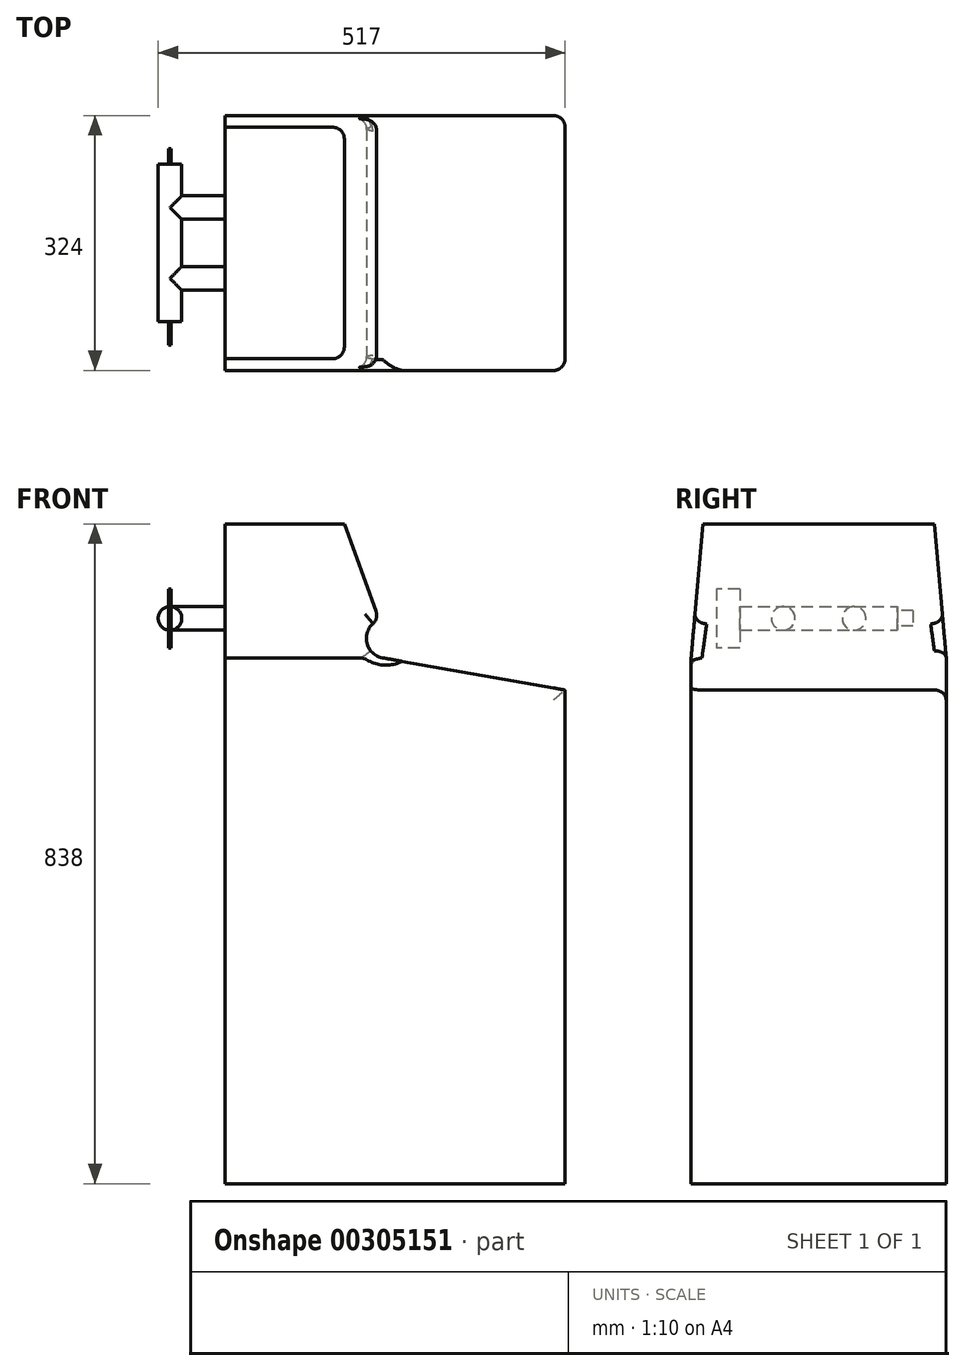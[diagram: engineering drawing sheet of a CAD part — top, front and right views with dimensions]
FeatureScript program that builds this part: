
annotation { "Feature Type Name" : "Feature", "Feature Type Description" : "" }
export const myFeature = defineFeature(function(context is Context, id is Id, definition is map)
    precondition{}
    {
        {
            var Q0;
            Q0=qCreatedBy(makeId("Top.planeOp"),FACE);
            var sketch = newSketch(context, id + "F0", { "sketchPlane" : qUnion([Q0])});
            skLineSegment(sketch, "E0.bottom", {"start": v(0, 162) * mm, "end": v(432, 162) * mm});
            skLineSegment(sketch, "E0.top", {"start": v(0, -162) * mm, "end": v(432, -162) * mm});
            skLineSegment(sketch, "E0.left", {"start": v(0, 162) * mm, "end": v(0, -162) * mm});
            skLineSegment(sketch, "E0.right", {"start": v(432, 162) * mm, "end": v(432, -162) * mm});
            skSolve(sketch);
        }
        {
            var Q0;
            Q0 = qSketchRegion(id + "F0", true);
            extrude(context, id + "F1", {"entities" : qUnion([Q0]), "depth" : 838 * mm});
        }
        {
            var Q0;
            Q0=makeQuery(id+"F1.opExtrude","SWEPT_FACE",FACE,{"disambiguationData":[OSD([sQuery(id+"F0.wireOp",EDGE,"E0.top")])]});
            var sketch = newSketch(context, id + "F2", { "sketchPlane" : qUnion([Q0])});
            skLineSegment(sketch, "E1", {"start": v(200, 668) * mm, "end": v(432, 627.1) * mm});
            skLineSegment(sketch, "E2", {"start": v(432, 627.1) * mm, "end": v(432, 838) * mm});
            skLineSegment(sketch, "E3", {"start": v(432, 838) * mm, "end": v(151.43, 838) * mm});
            skLineSegment(sketch, "E4", {"start": v(151.43, 838) * mm, "end": v(195.8, 716.11) * mm});
            skArc(sketch, "E5", {"start": v(200, 668) * mm, "mid": v(179.44, 690.44) * mm, "end": v(195.8, 716.11) * mm});
            skSolve(sketch);
        }
        {
            var Q0;
            Q0 = qSketchRegion(id + "F2", true);
            extrude(context, id + "F3", {"entities" : qUnion([Q0]), "operationType" : NewBodyOperationType.REMOVE, "endBound" : BoundingType.THROUGH_ALL, "oppositeDirection" : true, "depth" : 25 * mm});
        }
        {
            var Q0;
            Q0=makeQuery(id+"F1.opExtrude","SWEPT_FACE",FACE,{"disambiguationData":[OSD([sQuery(id+"F0.wireOp",EDGE,"E0.left")])]});
            var sketch = newSketch(context, id + "F4", { "sketchPlane" : qUnion([Q0])});
            skLineSegment(sketch, "E6", {"start": v(147.13, 838) * mm, "end": v(162, 838) * mm});
            skLineSegment(sketch, "E7", {"start": v(162, 838) * mm, "end": v(162, 668) * mm});
            skLineSegment(sketch, "E8", {"start": v(162, 668) * mm, "end": v(147.13, 838) * mm});
            skLineSegment(sketch, "E9", {"start": v(-162, 838) * mm, "end": v(-147.13, 838) * mm});
            skLineSegment(sketch, "E10", {"start": v(-147.13, 838) * mm, "end": v(-162, 668) * mm});
            skLineSegment(sketch, "E11", {"start": v(-162, 668) * mm, "end": v(-162, 838) * mm});
            skLineSegment(sketch, "E12.0", {"start": v(-162, 668) * mm, "end": v(162, 668) * mm, "construction": true});
            skSolve(sketch);
        }
        {
            var Q0;
            Q0 = qSketchRegion(id + "F4", true);
            extrude(context, id + "F5", {"entities" : qUnion([Q0]), "operationType" : NewBodyOperationType.REMOVE, "endBound" : BoundingType.THROUGH_ALL, "oppositeDirection" : true, "depth" : 25 * mm});
        }
        {
            var Q0;
            Q0=makeQuery(id+"F3.boolean.opBoolean","COPY",EDGE,{"derivedFrom":makeQuery(id+"F3.opExtrude","SWEPT_EDGE",EDGE,{"disambiguationData":[OSD([sQuery(id+"F0.wireOp",EDGE,"E0.top"),sQuery(id+"F2.wireOp",EDGE,"E3"),sQuery(id+"F2.wireOp",EDGE,"E4")])]})});
            var Q1;
            Q1=makeQuery(id+"F5.boolean.opBoolean","COPY",EDGE,{"derivedFrom":makeQuery(id+"F5.opExtrude","SWEPT_EDGE",EDGE,{"disambiguationData":[OSD([sQuery(id+"F0.wireOp",EDGE,"E0.left"),sQuery(id+"F4.wireOp",EDGE,"E6"),sQuery(id+"F4.wireOp",EDGE,"E8")])]})});
            var Q2;
            Q2=makeQuery(id+"F5.boolean.opBoolean","COPY",EDGE,{"derivedFrom":makeQuery(id+"F5.opExtrude","SWEPT_EDGE",EDGE,{"disambiguationData":[OSD([sQuery(id+"F0.wireOp",EDGE,"E0.left"),sQuery(id+"F4.wireOp",EDGE,"E9"),sQuery(id+"F4.wireOp",EDGE,"E10")])]})});
            var Q3;
            Q3=makeQuery(id+"F5.boolean.opBoolean","INTERSECT",EDGE,{"derivedFrom":[makeQuery(id+"F3.boolean.opBoolean","COPY",FACE,{"derivedFrom":makeQuery(id+"F3.opExtrude","SWEPT_FACE",FACE,{"disambiguationData":[OSD([sQuery(id+"F2.wireOp",EDGE,"E4")])]})}),makeQuery(id+"F5.opExtrude","SWEPT_FACE",FACE,{"disambiguationData":[OSD([sQuery(id+"F4.wireOp",EDGE,"E10")])]})]});
            var Q4;
            Q4=makeQuery(id+"F5.boolean.opBoolean","INTERSECT",EDGE,{"derivedFrom":[makeQuery(id+"F3.boolean.opBoolean","COPY",FACE,{"derivedFrom":makeQuery(id+"F3.opExtrude","SWEPT_FACE",FACE,{"disambiguationData":[OSD([sQuery(id+"F2.wireOp",EDGE,"E4")])]})}),makeQuery(id+"F5.opExtrude","SWEPT_FACE",FACE,{"disambiguationData":[OSD([sQuery(id+"F4.wireOp",EDGE,"E8")])]})]});
            var Q5;
            Q5=makeQuery(id+"F3.boolean.opBoolean","COPY",EDGE,{"derivedFrom":makeQuery(id+"F3.opExtrude","SWEPT_EDGE",EDGE,{"disambiguationData":[OSD([sQuery(id+"F2.wireOp",EDGE,"E4"),sQuery(id+"F2.wireOp",EDGE,"E5")])]})});
            var Q6;
            Q6=makeQuery(id+"F3.boolean.opBoolean","COPY",EDGE,{"derivedFrom":makeQuery(id+"F3.opExtrude","SWEPT_EDGE",EDGE,{"disambiguationData":[OSD([sQuery(id+"F2.wireOp",EDGE,"E1"),sQuery(id+"F2.wireOp",EDGE,"E5")])]})});
            var Q7;
            Q7=makeQuery(id+"F5.boolean.opBoolean","INTERSECT",EDGE,{"derivedFrom":[makeQuery(id+"F3.boolean.opBoolean","COPY",FACE,{"derivedFrom":makeQuery(id+"F3.opExtrude","SWEPT_FACE",FACE,{"disambiguationData":[OSD([sQuery(id+"F2.wireOp",EDGE,"E5")])]})}),makeQuery(id+"F5.opExtrude","SWEPT_FACE",FACE,{"disambiguationData":[OSD([sQuery(id+"F4.wireOp",EDGE,"E8")])]})]});
            var Q8;
            Q8=makeQuery(id+"F5.boolean.opBoolean","INTERSECT",EDGE,{"derivedFrom":[makeQuery(id+"F3.boolean.opBoolean","COPY",FACE,{"derivedFrom":makeQuery(id+"F3.opExtrude","SWEPT_FACE",FACE,{"disambiguationData":[OSD([sQuery(id+"F2.wireOp",EDGE,"E5")])]})}),makeQuery(id+"F5.opExtrude","SWEPT_FACE",FACE,{"disambiguationData":[OSD([sQuery(id+"F4.wireOp",EDGE,"E10")])]})]});
            var Q9;
            Q9=makeQuery(id+"F3.boolean.opBoolean","COPY",EDGE,{"derivedFrom":makeQuery(id+"F3.opExtrude","CAP_EDGE",EDGE,{"disambiguationData":[OSD([sQuery(id+"F2.wireOp",EDGE,"E1")])],"isStart":true})});
            var Q10;
            Q10=makeQuery(id+"F3.boolean.opBoolean","INTERSECT",EDGE,{"derivedFrom":[makeQuery(id+"F1.opExtrude","SWEPT_FACE",FACE,{"disambiguationData":[OSD([sQuery(id+"F0.wireOp",EDGE,"E0.bottom")])]}),makeQuery(id+"F3.opExtrude","SWEPT_FACE",FACE,{"disambiguationData":[OSD([sQuery(id+"F2.wireOp",EDGE,"E1")])]})]});
            var Q11;
            Q11=makeQuery(id+"F3.boolean.opBoolean","COPY",EDGE,{"derivedFrom":makeQuery(id+"F3.opExtrude","SWEPT_EDGE",EDGE,{"disambiguationData":[OSD([sQuery(id+"F0.wireOp",EDGE,"E0.top"),sQuery(id+"F0.wireOp",EDGE,"E0.right"),sQuery(id+"F2.wireOp",EDGE,"E1"),sQuery(id+"F2.wireOp",EDGE,"E2")])]})});
            var Q12;
            Q12=makeQuery(id+"F1.opExtrude","SWEPT_EDGE",EDGE,{"disambiguationData":[OSD([sQuery(id+"F0.wireOp",EDGE,"E0.top"),sQuery(id+"F0.wireOp",EDGE,"E0.right")])]});
            var Q13;
            Q13=makeQuery(id+"F1.opExtrude","SWEPT_EDGE",EDGE,{"disambiguationData":[OSD([sQuery(id+"F0.wireOp",EDGE,"E0.bottom"),sQuery(id+"F0.wireOp",EDGE,"E0.right")])]});
            fillet(context, id + "F6", {"entities" : qUnion([Q0, Q1, Q2, Q3, Q4, Q5, Q6, Q7, Q8, Q9, Q10, Q11, Q12, Q13]), "radius" : 15 * mm, "tangentPropagation" : true, "allowEdgeOverflow" : false});
        }
        {
            var Q0;
            Q0=makeQuery(id+"F1.opExtrude","SWEPT_FACE",FACE,{"disambiguationData":[OSD([sQuery(id+"F0.wireOp",EDGE,"E0.left")])]});
            var sketch = newSketch(context, id + "F7", { "sketchPlane" : qUnion([Q0])});
            skCircle(sketch, "E13", {"center": v(-45, 718.12) * mm, "radius": 15 * mm});
            skCircle(sketch, "E14", {"center": v(45, 718.12) * mm, "radius": 15 * mm});
            skSolve(sketch);
        }
        {
            var Q0;
            Q0 = qSketchRegion(id + "F7", true);
            extrude(context, id + "F8", {"entities" : qUnion([Q0]), "operationType" : NewBodyOperationType.ADD, "depth" : 70 * mm});
        }
        {
            var Q0;
            Q0=qCreatedBy(makeId("Front.planeOp"),FACE);
            var sketch = newSketch(context, id + "F9", { "sketchPlane" : qUnion([Q0])});
            skCircle(sketch, "E15", {"center": v(-70, 718.12) * mm, "radius": 15 * mm});
            skLineSegment(sketch, "E16.0.0", {"start": v(-70, 703.12) * mm, "end": v(-70, 733.12) * mm, "construction": true});
            skSolve(sketch);
        }
        {
            var Q0;
            Q0 = qSketchRegion(id + "F9", true);
            extrude(context, id + "F10", {"entities" : qUnion([Q0]), "operationType" : NewBodyOperationType.ADD, "endBound" : BoundingType.SYMMETRIC, "depth" : 200 * mm});
        }
        {
            var Q0;
            Q0=qCreatedBy(makeId("Right.planeOp"),FACE);
            var Q1;
            Q1=makeQuery(id+"F10.boolean.opBoolean","INTERSECT",VERTEX,{"disambiguationData":[OD(1.0)],"derivedFrom":[makeQuery(id+"F8.opExtrude","SWEPT_FACE",FACE,{"disambiguationData":[OSD([sQuery(id+"F7.wireOp",EDGE,"E14")])]}),makeQuery(id+"F10.opExtrude","SWEPT_FACE",FACE,{"disambiguationData":[OSD([sQuery(id+"F9.wireOp",EDGE,"E15")])]})]});
            cPlane(context, id + "F11", {"entities" : qUnion([Q0, Q1]), "cplaneType" : CPlaneType.PLANE_POINT, "offset" : 25 * mm, "width" : 150 * mm, "height" : 150 * mm});
        }
        {
            var Q0;
            Q0=qCreatedBy(id+"F11.planeOp",FACE);
            var sketch = newSketch(context, id + "F12", { "sketchPlane" : qUnion([Q0])});
            skLineSegment(sketch, "E17.bottom", {"start": v(-100, 755.62) * mm, "end": v(-130, 755.62) * mm});
            skLineSegment(sketch, "E17.top", {"start": v(-100, 680.62) * mm, "end": v(-130, 680.62) * mm});
            skLineSegment(sketch, "E17.left", {"start": v(-100, 755.62) * mm, "end": v(-100, 680.62) * mm});
            skLineSegment(sketch, "E17.right", {"start": v(-130, 755.62) * mm, "end": v(-130, 680.62) * mm});
            skLineSegment(sketch, "E18.bottom", {"start": v(120, 728.12) * mm, "end": v(100, 728.12) * mm});
            skLineSegment(sketch, "E18.top", {"start": v(120, 708.12) * mm, "end": v(100, 708.12) * mm});
            skLineSegment(sketch, "E18.left", {"start": v(120, 728.12) * mm, "end": v(120, 708.12) * mm});
            skLineSegment(sketch, "E18.right", {"start": v(100, 728.12) * mm, "end": v(100, 708.12) * mm});
            skLineSegment(sketch, "E19.0", {"start": v(100, 703.12) * mm, "end": v(100, 733.12) * mm, "construction": true});
            skLineSegment(sketch, "E20.0.0", {"start": v(-100, 703.12) * mm, "end": v(-100, 733.12) * mm, "construction": true});
            skLineSegment(sketch, "E21", {"start": v(-100, 718.12) * mm, "end": v(100, 718.12) * mm, "construction": true});
            skSolve(sketch);
        }
        {
            var Q0;
            Q0 = qSketchRegion(id + "F12", true);
            extrude(context, id + "F13", {"entities" : qUnion([Q0]), "operationType" : NewBodyOperationType.ADD, "endBound" : BoundingType.SYMMETRIC, "depth" : 3 * mm});
        }
    });
